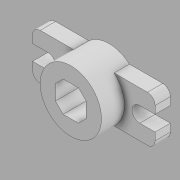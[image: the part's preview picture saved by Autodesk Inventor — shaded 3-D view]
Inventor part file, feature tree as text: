
AUTODESK INVENTOR PART (.ipt)
format: ipt  version: 2020 (Build 240168000, 168)  size: 146,432 bytes
history: native  units: mm
features: extrude x3, sketch x3, other x1, fillet x1
ambient origin geometry x8: Origin, YZ Plane, XZ Plane, XY Plane, X Axis, Y Axis, Z Axis, Center Point
bodies: Body1 (feature_tree)
feature tree (8):
  other  "Sólido1"
  extrude  "Extrusión1"  Depth=60.0mm
  extrude  "Extrusión2"  Depth=20.0mm
  extrude  "Extrusión3"  Depth=20.0mm
  fillet  "Empalme1"  Radius=20.0mm
  sketch  "Boceto1"  dims[d2=160.0mm d3=60.0mm]
  sketch  "Boceto2"  dims[d4=20.0mm d5=20.0mm]
  sketch  "Boceto3"  dims[d6=20.0mm d7=20.0mm d8=20.0mm d9=0.0mm d10=80.0mm d11=30.0mm d12=20.0mm d13=0.0mm d14=0.0mm d15=40.0mm d16=40.0mm d17=10.0mm d18=10.0mm d19=10.0mm d20=10.0mm d21=10.0mm d22=10.0mm d23=10.0mm d24=10.0mm d25=0.0mm d26=0.0mm d27=10.0mm]
